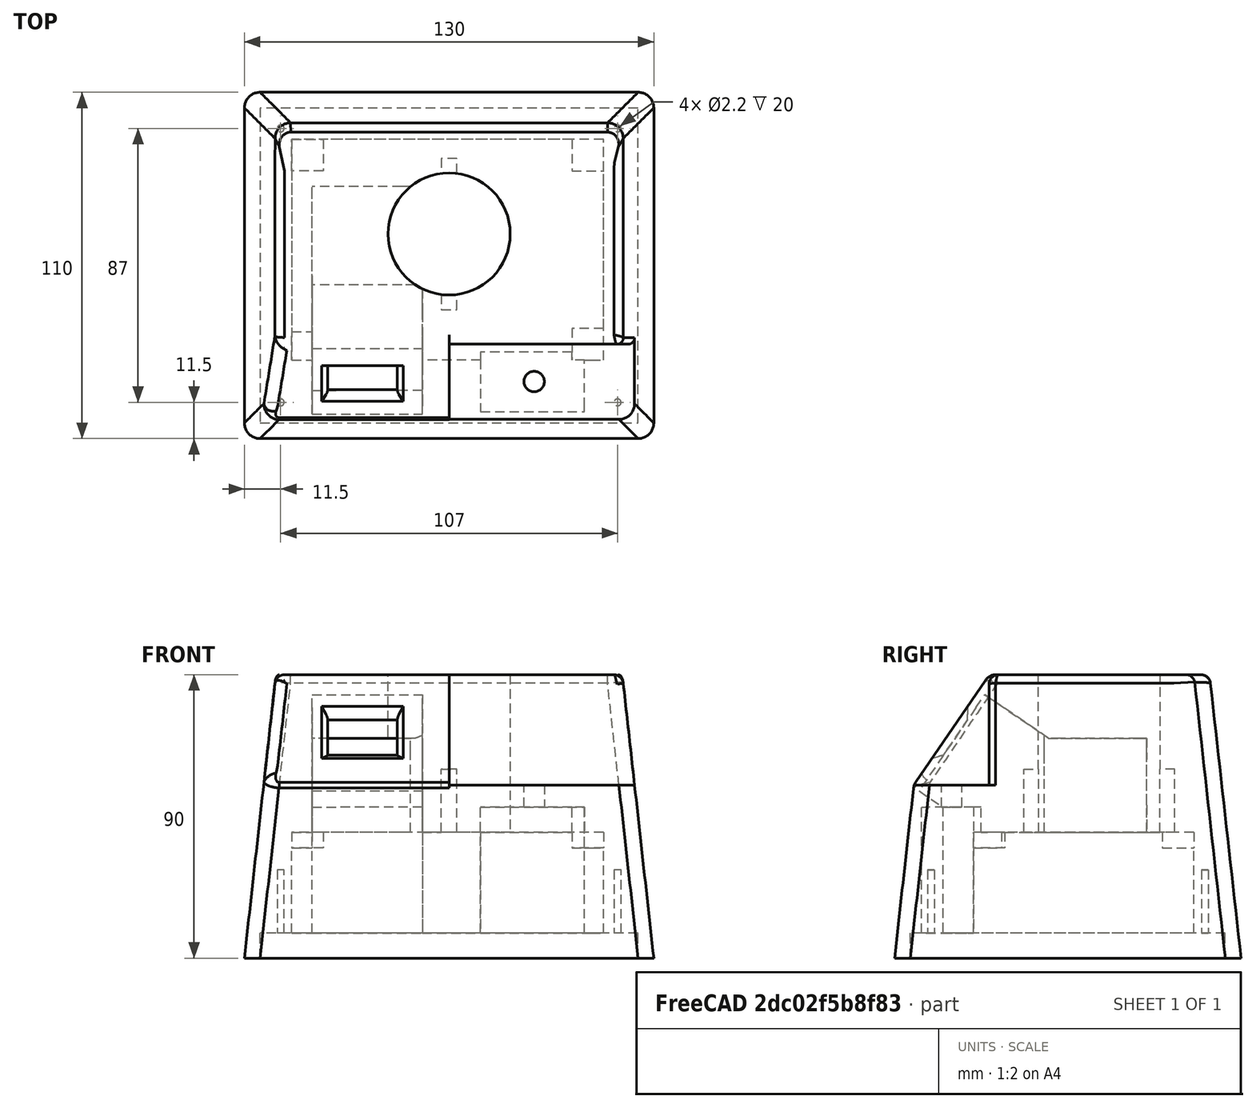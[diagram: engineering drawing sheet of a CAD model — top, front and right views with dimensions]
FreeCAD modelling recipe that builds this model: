
FCSTD DOCUMENT  (FreeCAD 0.17R13541 (Git))
Label: newDesign
License: All rights reserved
LicenseURL: http://en.wikipedia.org/wiki/All_rights_reserved
objects: PartDesign::Pocket×33, Sketcher::SketchObject×31, PartDesign::Plane×17, PartDesign::Pad×11, PartDesign::Fillet×9, PartDesign::Chamfer×2, PartDesign::AdditiveLoft×1, PartDesign::Body×1, Mesh::Feature×1
note: 150 computed .brp shape members not serialized (recipe doc carries the construction recipe); baked Part::Feature solids carry a one-line shape summary decoded from their .brp

FEATURE [Sketcher::SketchObject] Sketch
  MapMode = 5
  Support = -> [XY_Plane]
  sketch-geometry (4):
    g0: LineSegment StartX=0 StartY=110 StartZ=0 EndX=130 EndY=110 EndZ=0
    g1: LineSegment StartX=130 StartY=110 StartZ=0 EndX=130 EndY=0 EndZ=0
    g2: LineSegment StartX=130 StartY=0 StartZ=0 EndX=0 EndY=0 EndZ=0
    g3: LineSegment StartX=0 StartY=0 StartZ=0 EndX=0 EndY=110 EndZ=0
  constraints (11):
    c: Coincident(g0,g1)
    c: Coincident(g1,g2)
    c: Coincident(g2,g3)
    c: Coincident(g3,g0)
    c: Horizontal(g0)
    c: Horizontal(g2)
    c: Vertical(g1)
    c: Vertical(g3)
    c: Distance(g0) = 130
    c: Distance(g1) = 110
    c: Coincident(g-1,g2)
FEATURE [PartDesign::Plane] DatumPlane
  AttachmentOffset = pos=(0,90,0) rot=(1,0,0;1.5708rad)
  MapMode = 7
  Placement = pos=(0,110,90) rot=(0.707107,-0.707107,0;3.14159rad)
  Support = -> [Sketch]
FEATURE [Sketcher::SketchObject] Sketch001
  MapMode = 5
  Placement = pos=(0,110,90) rot=(-0.707107,0.707107,0;3.14159rad)
  Support = -> [DatumPlane]
  sketch-geometry (4):
    g0: LineSegment StartX=10 StartY=-10 StartZ=0 EndX=100 EndY=-10 EndZ=0
    g1: LineSegment StartX=100 StartY=-10 StartZ=0 EndX=100 EndY=-120 EndZ=0
    g2: LineSegment StartX=100 StartY=-120 StartZ=0 EndX=10 EndY=-120 EndZ=0
    g3: LineSegment StartX=10 StartY=-120 StartZ=0 EndX=10 EndY=-10 EndZ=0
  constraints (12):
    c: Coincident(g0,g1)
    c: Coincident(g1,g2)
    c: Coincident(g2,g3)
    c: Coincident(g3,g0)
    c: Horizontal(g0)
    c: Horizontal(g2)
    c: Vertical(g1)
    c: Vertical(g3)
    c: DistanceX(g0,g0) = 90
    c: DistanceY(g1,g1) = 110
    c: DistanceY(g0,g-1) = 10
    c: DistanceX(g-1,g0) = 10
FEATURE [PartDesign::AdditiveLoft] AdditiveLoft
  Closed = false
  Profile = -> Sketch
  Ruled = false
  Sections = -> [Sketch001]
FEATURE [PartDesign::Plane] DatumPlane001
  MapMode = 5
  Placement = pos=(0,0,90) rot=(0,0,1;0rad)
  Support = -> [AdditiveLoft]
FEATURE [Sketcher::SketchObject] Sketch002
  MapMode = 5
  Placement = pos=(0,0,90) rot=(0,0,1;0rad)
  Support = -> [DatumPlane001]
  sketch-geometry (4):
    g0: LineSegment StartX=65 StartY=30 StartZ=0 EndX=130 EndY=30 EndZ=0
    g1: LineSegment StartX=130 StartY=30 StartZ=0 EndX=130 EndY=0 EndZ=0
    g2: LineSegment StartX=130 StartY=0 StartZ=0 EndX=65 EndY=0 EndZ=0
    g3: LineSegment StartX=65 StartY=0 StartZ=0 EndX=65 EndY=30 EndZ=0
  constraints (12):
    c: Coincident(g0,g1)
    c: Coincident(g1,g2)
    c: Coincident(g2,g3)
    c: Coincident(g3,g0)
    c: Horizontal(g0)
    c: Horizontal(g2)
    c: Vertical(g1)
    c: Vertical(g3)
    c: DistanceX(g-1,g2) = 65
    c: DistanceY(g1,g1) = 30
    c: DistanceY(g-1,g2) = 0
    c: DistanceX(g0,g0) = 65
FEATURE [PartDesign::Pocket] Pocket
  BaseFeature = -> AdditiveLoft
  Length = 35
  Length2 = 100
  Profile = -> Sketch002
  Type = 0
FEATURE [PartDesign::Plane] DatumPlane002
  MapMode = 5
  Placement = pos=(65,0,0) rot=(0.57735,0.57735,0.57735;2.0944rad)
  Support = -> [Pocket]
FEATURE [Sketcher::SketchObject] Sketch003
  ExternalGeometry = -> [Pocket]
  MapMode = 5
  Placement = pos=(65,0,0) rot=(0.57735,0.57735,0.57735;2.0944rad)
  Support = -> [DatumPlane002]
  sketch-geometry (3):
    g0: LineSegment StartX=6.11111 StartY=55 StartZ=0 EndX=30 EndY=90 EndZ=0
    g1: LineSegment StartX=30 StartY=90 StartZ=0 EndX=10 EndY=90 EndZ=0
    g2: LineSegment StartX=10 StartY=90 StartZ=0 EndX=6.11111 EndY=55 EndZ=0
  constraints (7):
    c: Coincident(g0,g1)
    c: Horizontal(g1)
    c: Coincident(g1,g2)
    c: Coincident(g2,g0)
    c: Coincident(g0,g-3)
    c: Coincident(g1,g-5)
    c: Coincident(g0,g-4)
FEATURE [PartDesign::Pocket] Pocket001
  BaseFeature = -> Pocket
  Length = 60
  Length2 = 100
  Profile = -> Sketch003
  Type = 0
FEATURE [Sketcher::SketchObject] Sketch004
  MapMode = 5
  Placement = pos=(0,0,55) rot=(0,0,1;0rad)
  Support = -> [Pocket001]
FEATURE [PartDesign::Plane] DatumPlane003
  MapMode = 5
  Placement = pos=(0,0,55) rot=(0,0,1;0rad)
  Support = -> [Pocket001]
FEATURE [Sketcher::SketchObject] Sketch005
  ExternalGeometry = -> [Pocket001]
  MapMode = 5
  Placement = pos=(0,0,55) rot=(0,0,1;0rad)
  Support = -> [DatumPlane003]
  sketch-geometry (1):
    g0: Circle CenterX=92 CenterY=18.1111 CenterZ=0 NormalX=0 NormalY=0 NormalZ=1 AngleXU=0 Radius=3.25
  constraints (3):
    c: Radius(g0) = 3.25
    c: DistanceX(g-3,g0) = 27
    c: DistanceY(g-3,g0) = 12
FEATURE [PartDesign::Pad] Pad
  BaseFeature = -> Pocket001
  Length = 10
  Length2 = 100
  Profile = -> Sketch005
  Type = 0
FEATURE [PartDesign::Plane] DatumPlane004
  MapMode = 5
  Placement = pos=(0,-21.4404,14.6339) rot=(1,0,0;0.971885rad)
  Support = -> [Pad]
FEATURE [Sketcher::SketchObject] Sketch006
  ExternalGeometry = -> [Pad]
  MapMode = 5
  Placement = pos=(0,-21.4404,14.6339) rot=(1,0,0;0.971885rad)
  Support = -> [DatumPlane004]
  sketch-geometry (4):
    g0: LineSegment StartX=26.5 StartY=74.6655 StartZ=0 EndX=48.5 EndY=74.6655 EndZ=0
    g1: LineSegment StartX=48.5 StartY=74.6655 StartZ=0 EndX=48.5 EndY=62.6655 EndZ=0
    g2: LineSegment StartX=48.5 StartY=62.6655 StartZ=0 EndX=26.5 EndY=62.6655 EndZ=0
    g3: LineSegment StartX=26.5 StartY=62.6655 StartZ=0 EndX=26.5 EndY=74.6655 EndZ=0
  constraints (11):
    c: Coincident(g0,g1)
    c: Coincident(g1,g2)
    c: Coincident(g2,g3)
    c: Coincident(g3,g0)
    c: Horizontal(g0)
    c: Horizontal(g2)
    c: Vertical(g1)
    c: Vertical(g3)
    c: DistanceX(g0,g0) = 22
    c: DistanceY(g3,g3) = 12
    c: DistanceX(g-4,g0) = 16.5
FEATURE [PartDesign::Pocket] Pocket002
  BaseFeature = -> Pad
  Length = 3
  Length2 = 100
  Profile = -> Sketch006
  Type = 0
FEATURE [PartDesign::Plane] DatumPlane005
  MapMode = 5
  Placement = pos=(48.5,0,0) rot=(0.57735,-0.57735,-0.57735;2.0944rad)
  Support = -> [Pocket002]
FEATURE [Sketcher::SketchObject] Sketch007
  ExternalGeometry = -> [Pocket002]
  MapMode = 5
  Placement = pos=(48.5,0,0) rot=(0.57735,-0.57735,-0.57735;2.0944rad)
  Support = -> [DatumPlane005]
  sketch-geometry (4):
    g0: LineSegment StartX=-23.1297 StartY=74.6127 StartZ=0 EndX=-20.6519 EndY=76.3039 EndZ=0
    g1: LineSegment StartX=-20.6519 StartY=76.3039 StartZ=0 EndX=-20.6519 EndY=81.3039 EndZ=0
    g2: LineSegment StartX=-20.6519 StartY=81.3039 StartZ=0 EndX=-23.1297 EndY=81.3039 EndZ=0
    g3: LineSegment StartX=-23.1297 StartY=81.3039 StartZ=0 EndX=-23.1297 EndY=74.6127 EndZ=0
  constraints (10):
    c: Coincident(g0,g1)
    c: Vertical(g1)
    c: Coincident(g1,g2)
    c: Horizontal(g2)
    c: Coincident(g2,g3)
    c: Vertical(g3)
    c: Coincident(g3,g0)
    c: Coincident(g0,g-4)
    c: Coincident(g-3,g0)
    c: DistanceY(g1,g1) = 5
FEATURE [PartDesign::Pocket] Pocket003
  BaseFeature = -> Pocket002
  Length = 22
  Length2 = 100
  Profile = -> Sketch007
  Reversed = true
  Type = 0
FEATURE [PartDesign::Plane] DatumPlane006
  MapMode = 5
  Placement = pos=(48.5,0,0) rot=(0.57735,-0.57735,-0.57735;2.0944rad)
  Support = -> [Pocket003]
FEATURE [Sketcher::SketchObject] Sketch008
  MapMode = 5
  Placement = pos=(48.5,0,0) rot=(0.57735,-0.57735,-0.57735;2.0944rad)
  Support = -> [DatumPlane006]
FEATURE [Sketcher::SketchObject] Sketch009
  ExternalGeometry = -> [Pocket003]
  MapMode = 5
  Placement = pos=(48.5,0,0) rot=(0.57735,-0.57735,-0.57735;2.0944rad)
  Support = -> [DatumPlane006]
  sketch-geometry (3):
    g0: LineSegment StartX=-16.3648 StartY=64.7013 StartZ=0 EndX=-16.3648 EndY=74.7013 EndZ=0
    g1: LineSegment StartX=-16.3648 StartY=74.7013 StartZ=0 EndX=-7.90863 EndY=62.312 EndZ=0
    g2: LineSegment StartX=-7.90863 StartY=62.312 StartZ=0 EndX=-16.3648 EndY=64.7013 EndZ=0
  constraints (8):
    c: Vertical(g0)
    c: Coincident(g0,g1)
    c: Coincident(g2,g0)
    c: Parallel(g1,g-4)
    c: Distance(g0) = 10
    c: Coincident(g0,g-3)
    c: Coincident(g2,g1)
    c: Distance(g1) = 15
FEATURE [PartDesign::Pocket] Pocket004
  BaseFeature = -> Pocket003
  Length = 22
  Length2 = 100
  Profile = -> Sketch009
  Reversed = true
  Type = 0
FEATURE [PartDesign::Chamfer] Chamfer
  Base = -> Pocket004 [Edge26,Edge27,Edge28,Edge29]
  BaseFeature = -> Pocket004
  Size = 2
FEATURE [PartDesign::Fillet] Fillet
  Base = -> Chamfer [Edge31,Edge27,Edge24,Edge21]
  BaseFeature = -> Chamfer
  Radius = 2
FEATURE [PartDesign::Chamfer] Chamfer001
  Base = -> Fillet [Edge22,Edge20,Edge17,Edge24]
  BaseFeature = -> Fillet
  Size = 2
FEATURE [PartDesign::Fillet] Fillet001
  Base = -> Chamfer001 [Edge10,Edge36,Edge44,Edge54]
  BaseFeature = -> Chamfer001
  Radius = 2
FEATURE [PartDesign::Fillet] Fillet002
  Base = -> Fillet001 [Edge91]
  BaseFeature = -> Fillet001
  Radius = 5
FEATURE [PartDesign::Fillet] Fillet003
  Base = -> Fillet002 [Edge17]
  BaseFeature = -> Fillet002
  Radius = 5
FEATURE [PartDesign::Fillet] Fillet004
  Base = -> Fillet003 [Edge18]
  BaseFeature = -> Fillet003
  Radius = 2
FEATURE [PartDesign::Fillet] Fillet005
  Base = -> Fillet004 [Edge43]
  BaseFeature = -> Fillet004
  Radius = 5
FEATURE [PartDesign::Fillet] Fillet006
  Base = -> Fillet005 [Edge23]
  BaseFeature = -> Fillet005
  Radius = 5
FEATURE [PartDesign::Plane] DatumPlane007
  MapMode = 5
  Placement = pos=(0,0,90) rot=(0,0,1;0rad)
  Support = -> [Fillet006]
FEATURE [Sketcher::SketchObject] Sketch010
  ExternalGeometry = -> [Sketch001,Fillet006]
  MapMode = 5
  Placement = pos=(0,0,90) rot=(0,0,1;0rad)
  Support = -> [DatumPlane007]
  sketch-geometry (1):
    g0: Circle CenterX=65 CenterY=65 CenterZ=0 NormalX=0 NormalY=0 NormalZ=1 AngleXU=0 Radius=2
  constraints (3):
    c: Radius(g0) = 2
    c: DistanceX(g-3,g0) = 55
    c: DistanceY(g-6,g0) = 35
FEATURE [PartDesign::Pad] Pad001
  BaseFeature = -> Fillet006
  Length = 10
  Length2 = 100
  Profile = -> Sketch010
  Type = 0
FEATURE [PartDesign::Plane] DatumPlane008
  MapMode = 5
  Placement = pos=(0,0,100) rot=(0,0,1;0rad)
  Support = -> [Pad001]
FEATURE [Sketcher::SketchObject] Sketch011
  ExternalGeometry = -> [Pad001]
  MapMode = 5
  Placement = pos=(0,0,100) rot=(0,0,1;0rad)
  Support = -> [DatumPlane008]
  sketch-geometry (1):
    g0: Circle CenterX=65 CenterY=65 CenterZ=0 NormalX=0 NormalY=0 NormalZ=1 AngleXU=0 Radius=19.4
  constraints (2):
    c: Coincident(g0,g-3)
    c: Radius(g0) = 19.4
FEATURE [PartDesign::Pocket] Pocket005
  BaseFeature = -> Pad001
  Length = 100
  Length2 = 100
  Profile = -> Sketch011
  Type = 0
FEATURE [Sketcher::SketchObject] Sketch012
  MapMode = 5
  Placement = pos=(0,0,65) rot=(0,0,1;0rad)
  Support = -> [Pocket005]
FEATURE [PartDesign::Pocket] Pocket006
  BaseFeature = -> Pocket005
  Length = 68
  Length2 = 100
  Profile = -> Pocket005 [Face28]
  Type = 0
FEATURE [PartDesign::Plane] DatumPlane009
  MapMode = 5
  Placement = pos=(0,0,0) rot=(1,0,0;3.14159rad)
  Support = -> [Pocket006]
FEATURE [Sketcher::SketchObject] Sketch013
  MapMode = 5
  Placement = pos=(0,0,0) rot=(1,0,0;3.14159rad)
  Support = -> [DatumPlane009]
  sketch-geometry (4):
    g0: LineSegment StartX=15 StartY=-25 StartZ=0 EndX=114 EndY=-25 EndZ=0
    g1: LineSegment StartX=114 StartY=-25 StartZ=0 EndX=114 EndY=-95 EndZ=0
    g2: LineSegment StartX=114 StartY=-95 StartZ=0 EndX=15 EndY=-95 EndZ=0
    g3: LineSegment StartX=15 StartY=-95 StartZ=0 EndX=15 EndY=-25 EndZ=0
  constraints (12):
    c: Coincident(g0,g1)
    c: Coincident(g1,g2)
    c: Coincident(g2,g3)
    c: Coincident(g3,g0)
    c: Horizontal(g0)
    c: Horizontal(g2)
    c: Vertical(g1)
    c: Vertical(g3)
    c: DistanceX(g0,g0) = 99
    c: DistanceY(g1,g1) = 70
    c: DistanceY(g0,g-1) = 25
    c: DistanceX(g-1,g0) = 15
FEATURE [PartDesign::Pocket] Pocket007
  BaseFeature = -> Pocket006
  Length = 40
  Length2 = 100
  Profile = -> Sketch013
  Type = 0
FEATURE [PartDesign::Pocket] Pocket008
  BaseFeature = -> Pocket007
  Length = 64
  Length2 = 100
  Profile = -> Pocket007 [Face34]
  Type = 0
FEATURE [PartDesign::Plane] DatumPlane010
  MapMode = 5
  Placement = pos=(0,0,0) rot=(1,0,0;3.14159rad)
  Support = -> [Pocket008]
FEATURE [Sketcher::SketchObject] Sketch014
  MapMode = 5
  Placement = pos=(0,0,0) rot=(1,0,0;3.14159rad)
  Support = -> [DatumPlane010]
  sketch-geometry (4):
    g0: LineSegment StartX=75 StartY=-10 StartZ=0 EndX=110 EndY=-10 EndZ=0
    g1: LineSegment StartX=110 StartY=-10 StartZ=0 EndX=110 EndY=-27.5 EndZ=0
    g2: LineSegment StartX=110 StartY=-27.5 StartZ=0 EndX=75 EndY=-27.5 EndZ=0
    g3: LineSegment StartX=75 StartY=-27.5 StartZ=0 EndX=75 EndY=-10 EndZ=0
  constraints (12):
    c: Coincident(g0,g1)
    c: Coincident(g1,g2)
    c: Coincident(g2,g3)
    c: Coincident(g3,g0)
    c: Horizontal(g0)
    c: Horizontal(g2)
    c: Vertical(g1)
    c: Vertical(g3)
    c: DistanceX(g0,g0) = 35
    c: DistanceX(g-1,g0) = 75
    c: DistanceY(g1,g1) = 17.5
    c: DistanceY(g0,g-1) = 10
FEATURE [PartDesign::Pocket] Pocket009
  BaseFeature = -> Pocket008
  Length = 48
  Length2 = 100
  Profile = -> Sketch014
  Type = 0
FEATURE [PartDesign::Plane] DatumPlane011
  MapMode = 5
  Placement = pos=(0,0,40) rot=(1,0,0;3.14159rad)
  Support = -> [Pocket009]
FEATURE [Sketcher::SketchObject] Sketch015
  ExternalGeometry = -> [Pocket009]
  MapMode = 5
  Placement = pos=(0,0,40) rot=(1,0,0;3.14159rad)
  Support = -> [DatumPlane011]
  sketch-geometry (4):
    g0: LineSegment StartX=20 StartY=-40 StartZ=0 EndX=50 EndY=-40 EndZ=0
    g1: LineSegment StartX=50 StartY=-40 StartZ=0 EndX=50 EndY=-80 EndZ=0
    g2: LineSegment StartX=50 StartY=-80 StartZ=0 EndX=20 EndY=-80 EndZ=0
    g3: LineSegment StartX=20 StartY=-80 StartZ=0 EndX=20 EndY=-40 EndZ=0
  constraints (12):
    c: Coincident(g0,g1)
    c: Coincident(g1,g2)
    c: Coincident(g2,g3)
    c: Coincident(g3,g0)
    c: Horizontal(g0)
    c: Horizontal(g2)
    c: Vertical(g1)
    c: Vertical(g3)
    c: DistanceX(g0,g0) = 30
    c: DistanceX(g-3,g0) = 5
    c: DistanceY(g1,g1) = 40
    c: DistanceY(g0,g-3) = 15
FEATURE [PartDesign::Pocket] Pocket010
  BaseFeature = -> Pocket009
  Length = 31
  Length2 = 100
  Profile = -> Sketch015
  Type = 0
FEATURE [Sketcher::SketchObject] Sketch016
  ExternalGeometry = -> [Pocket010]
  MapMode = 5
  Placement = pos=(26.5,0,0) rot=(0.57735,0.57735,0.57735;2.0944rad)
  Support = -> [Pocket010]
  sketch-geometry (3):
    g0: LineSegment StartX=40 StartY=63.098 StartZ=0 EndX=33.2351 EndY=53.1866 EndZ=0
    g1: LineSegment StartX=33.2351 StartY=53.1866 StartZ=0 EndX=40 EndY=48.5693 EndZ=0
    g2: LineSegment StartX=40 StartY=48.5693 StartZ=0 EndX=40 EndY=63.098 EndZ=0
  constraints (7):
    c: Coincident(g0,g1)
    c: Coincident(g1,g2)
    c: Coincident(g2,g0)
    c: Coincident(g0,g-5)
    c: Coincident(g-4,g1)
    c: Parallel(g0,g-3)
    c: Parallel(g1,g-6)
FEATURE [PartDesign::Pocket] Pocket011
  BaseFeature = -> Pocket010
  Length = 5
  Length2 = 100
  Profile = -> Sketch016
  Type = 0
FEATURE [PartDesign::Plane] DatumPlane012
  MapMode = 5
  Placement = pos=(0,-2.09222,1.42802) rot=(0,0.884235,0.467042;3.14159rad)
  Support = -> [Pocket011]
FEATURE [Sketcher::SketchObject] Sketch017
  ExternalGeometry = -> [Pocket011]
  MapMode = 5
  Placement = pos=(0,-2.09222,1.42802) rot=(0,0.884235,0.467042;3.14159rad)
  Support = -> [DatumPlane012]
  sketch-geometry (4):
    g0: LineSegment StartX=-21.5 StartY=74.6655 StartZ=0 EndX=-56.5 EndY=74.6655 EndZ=0
    g1: LineSegment StartX=-56.5 StartY=74.6655 StartZ=0 EndX=-56.5 EndY=49.6655 EndZ=0
    g2: LineSegment StartX=-56.5 StartY=49.6655 StartZ=0 EndX=-21.5 EndY=49.6655 EndZ=0
    g3: LineSegment StartX=-21.5 StartY=49.6655 StartZ=0 EndX=-21.5 EndY=74.6655 EndZ=0
  constraints (11):
    c: Coincident(g0,g1)
    c: Coincident(g1,g2)
    c: Coincident(g2,g3)
    c: Coincident(g3,g0)
    c: Horizontal(g0)
    c: Horizontal(g2)
    c: Vertical(g1)
    c: Vertical(g3)
    c: Coincident(g0,g-3)
    c: DistanceX(g0,g0) = 35
    c: DistanceY(g3,g3) = 25
FEATURE [PartDesign::Pocket] Pocket012
  BaseFeature = -> Pocket011
  Length = 25
  Length2 = 100
  Profile = -> Sketch017
  Reversed = true
  Type = 0
FEATURE [Sketcher::SketchObject] Sketch018
  ExternalGeometry = -> [Pocket012]
  MapMode = 5
  Placement = pos=(0,0,40) rot=(1,0,0;3.14159rad)
  Support = -> [Pocket012]
  sketch-geometry (4):
    g0: LineSegment StartX=56.5 StartY=-29.4949 StartZ=0 EndX=21.5 EndY=-29.4949 EndZ=0
    g1: LineSegment StartX=21.5 StartY=-29.4949 StartZ=0 EndX=21.5 EndY=-25 EndZ=0
    g2: LineSegment StartX=21.5 StartY=-25 StartZ=0 EndX=56.5 EndY=-25 EndZ=0
    g3: LineSegment StartX=56.5 StartY=-25 StartZ=0 EndX=56.5 EndY=-29.4949 EndZ=0
  constraints (11):
    c: Coincident(g0,g1)
    c: Coincident(g1,g2)
    c: Coincident(g2,g3)
    c: Coincident(g3,g0)
    c: Horizontal(g0)
    c: Horizontal(g2)
    c: Vertical(g1)
    c: Vertical(g3)
    c: Coincident(g0,g-3)
    c: Coincident(g0,g-4)
    c: DistanceY(g1,g-5) = 0
FEATURE [PartDesign::Pocket] Pocket013
  BaseFeature = -> Pocket012
  Length = 5
  Length2 = 100
  Profile = -> Sketch018
  Type = 0
FEATURE [Sketcher::SketchObject] Sketch019
  ExternalGeometry = -> [Pocket013]
  MapMode = 5
  Placement = pos=(0,-2.09222,1.42802) rot=(0,0.884235,0.467042;3.14159rad)
  Support = -> [Pocket013]
  sketch-geometry (4):
    g0: LineSegment StartX=-56.5 StartY=80.2538 StartZ=0 EndX=-21.5 EndY=80.2538 EndZ=0
    g1: LineSegment StartX=-21.5 StartY=80.2538 StartZ=0 EndX=-21.5 EndY=52.7538 EndZ=0
    g2: LineSegment StartX=-21.5 StartY=52.7538 StartZ=0 EndX=-56.5 EndY=52.7538 EndZ=0
    g3: LineSegment StartX=-56.5 StartY=52.7538 StartZ=0 EndX=-56.5 EndY=80.2538 EndZ=0
  constraints (11):
    c: Coincident(g0,g1)
    c: Coincident(g1,g2)
    c: Coincident(g2,g3)
    c: Coincident(g3,g0)
    c: Horizontal(g0)
    c: Horizontal(g2)
    c: Vertical(g1)
    c: Vertical(g3)
    c: Coincident(g-3,g2)
    c: DistanceX(g2,g2) = 35
    c: DistanceY(g1,g1) = 27.5
FEATURE [PartDesign::Pocket] Pocket014
  BaseFeature = -> Pocket013
  Length = 19
  Length2 = 100
  Profile = -> Sketch019
  Type = 0
FEATURE [PartDesign::Pocket] Pocket015
  BaseFeature = -> Pocket014
  Length = 20
  Length2 = 100
  Profile = -> Sketch019
  Reversed = true
  Type = 0
FEATURE [Sketcher::SketchObject] Sketch020
  ExternalGeometry = -> [Pocket015]
  MapMode = 5
  Placement = pos=(0,0,71) rot=(1,0,0;3.14159rad)
  Support = -> [Pocket015]
  sketch-geometry (4):
    g0: LineSegment StartX=20 StartY=-40 StartZ=0 EndX=56.5 EndY=-40 EndZ=0
    g1: LineSegment StartX=56.5 StartY=-40 StartZ=0 EndX=56.5 EndY=-80 EndZ=0
    g2: LineSegment StartX=56.5 StartY=-80 StartZ=0 EndX=20 EndY=-80 EndZ=0
    g3: LineSegment StartX=20 StartY=-80 StartZ=0 EndX=20 EndY=-40 EndZ=0
  constraints (11):
    c: Coincident(g0,g1)
    c: Coincident(g1,g2)
    c: Coincident(g2,g3)
    c: Coincident(g3,g0)
    c: Horizontal(g0)
    c: Horizontal(g2)
    c: Vertical(g1)
    c: Vertical(g3)
    c: Coincident(g2,g-4)
    c: Coincident(g-3,g0)
    c: DistanceX(g0,g-5) = 0
FEATURE [PartDesign::Pocket] Pocket016
  BaseFeature = -> Pocket015
  Length = 39
  Length2 = 100
  Profile = -> Sketch020
  Reversed = true
  Type = 0
FEATURE [PartDesign::Pad] Pad002
  BaseFeature = -> Pocket016
  Length = 40
  Length2 = 100
  Profile = -> Pocket016 [Face75]
  Type = 0
FEATURE [PartDesign::Pad] Pad003
  BaseFeature = -> Pad002
  Length = 40
  Length2 = 100
  Profile = -> Pad002 [Face80]
  Type = 0
FEATURE [PartDesign::Pocket] Pocket017
  BaseFeature = -> Pad003
  Length = 5
  Length2 = 100
  Profile = -> Pad003 [Face79]
  Type = 0
FEATURE [PartDesign::Pocket] Pocket018
  BaseFeature = -> Pocket017
  Length = 5
  Length2 = 100
  Profile = -> Pocket017 [Face60]
  Type = 0
FEATURE [PartDesign::Pocket] Pocket019
  BaseFeature = -> Pocket018
  Length = 5
  Length2 = 100
  Profile = -> Pocket018 [Face81]
  Type = 0
FEATURE [PartDesign::Pad] Pad004
  BaseFeature = -> Pocket019
  Length = 10
  Length2 = 100
  Profile = -> Pocket019 [Face83]
  Type = 0
FEATURE [PartDesign::Pocket] Pocket020
  BaseFeature = -> Pad004
  Length = 5
  Length2 = 100
  Profile = -> Pad004 [Face60]
  Type = 0
FEATURE [PartDesign::Pocket] Pocket021
  BaseFeature = -> Pocket020
  Length = 1
  Length2 = 100
  Profile = -> Pocket020 [Face65]
  Type = 0
FEATURE [PartDesign::Pocket] Pocket022
  BaseFeature = -> Pocket021
  Length = 1
  Length2 = 100
  Profile = -> Pocket021 [Face65]
  Type = 0
FEATURE [Sketcher::SketchObject] Sketch021
  ExternalGeometry = -> [Pocket022]
  MapMode = 5
  Placement = pos=(0,45.2426,66.2856) rot=(1,0,0;2.54268rad)
  Support = -> [Pocket022]
  sketch-geometry (4):
    g0: LineSegment StartX=21.5 StartY=23.5331 StartZ=0 EndX=56.5 EndY=23.5331 EndZ=0
    g1: LineSegment StartX=56.5 StartY=23.5331 StartZ=0 EndX=56.5 EndY=-1.46689 EndZ=0
    g2: LineSegment StartX=56.5 StartY=-1.46689 StartZ=0 EndX=21.5 EndY=-1.46689 EndZ=0
    g3: LineSegment StartX=21.5 StartY=-1.46689 StartZ=0 EndX=21.5 EndY=23.5331 EndZ=0
  constraints (11):
    c: Coincident(g0,g1)
    c: Coincident(g1,g2)
    c: Coincident(g2,g3)
    c: Coincident(g3,g0)
    c: Horizontal(g0)
    c: Horizontal(g2)
    c: Vertical(g1)
    c: Vertical(g3)
    c: Coincident(g0,g-3)
    c: Coincident(g0,g-4)
    c: DistanceY(g1,g1) = 25
FEATURE [PartDesign::Pocket] Pocket023
  BaseFeature = -> Pocket022
  Length = 5
  Length2 = 100
  Profile = -> Sketch021
  Type = 0
FEATURE [PartDesign::Plane] DatumPlane013
  MapMode = 5
  Placement = pos=(0,-19.4372,13.2666) rot=(0,0.884235,0.467042;3.14159rad)
  Support = -> [Pocket023]
FEATURE [Sketcher::SketchObject] Sketch022
  ExternalGeometry = -> [Pocket023]
  MapMode = 5
  Placement = pos=(0,-19.4372,13.2666) rot=(0,0.884235,0.467042;3.14159rad)
  Support = -> [DatumPlane013]
  sketch-geometry (4):
    g0: LineSegment StartX=-56.5 StartY=85.2538 StartZ=0 EndX=-21.5 EndY=85.2538 EndZ=0
    g1: LineSegment StartX=-21.5 StartY=85.2538 StartZ=0 EndX=-21.5 EndY=48.2538 EndZ=0
    g2: LineSegment StartX=-21.5 StartY=48.2538 StartZ=0 EndX=-56.5 EndY=48.2538 EndZ=0
    g3: LineSegment StartX=-56.5 StartY=48.2538 StartZ=0 EndX=-56.5 EndY=85.2538 EndZ=0
  constraints (11):
    c: Coincident(g0,g1)
    c: Coincident(g1,g2)
    c: Coincident(g2,g3)
    c: Coincident(g3,g0)
    c: Horizontal(g0)
    c: Horizontal(g2)
    c: Vertical(g1)
    c: Vertical(g3)
    c: Coincident(g0,g-3)
    c: Coincident(g0,g-4)
    c: DistanceY(g1,g1) = 37
FEATURE [PartDesign::Pocket] Pocket024
  BaseFeature = -> Pocket023
  Length = 28
  Length2 = 100
  Profile = -> Sketch022
  Reversed = true
  Type = 0
FEATURE [PartDesign::Plane] DatumPlane014
  MapMode = 5
  Placement = pos=(0,0,0) rot=(1,0,0;3.14159rad)
  Support = -> [Pocket024]
FEATURE [Sketcher::SketchObject] Sketch023
  ExternalGeometry = -> [Pocket024]
  MapMode = 5
  Placement = pos=(0,0,0) rot=(1,0,0;3.14159rad)
  Support = -> [DatumPlane014]
  sketch-geometry (4):
    g0: LineSegment StartX=75 StartY=-25 StartZ=0 EndX=30 EndY=-25 EndZ=0
    g1: LineSegment StartX=30 StartY=-25 StartZ=0 EndX=30 EndY=-10 EndZ=0
    g2: LineSegment StartX=30 StartY=-10 StartZ=0 EndX=75 EndY=-10 EndZ=0
    g3: LineSegment StartX=75 StartY=-10 StartZ=0 EndX=75 EndY=-25 EndZ=0
  constraints (11):
    c: Coincident(g0,g1)
    c: Coincident(g1,g2)
    c: Coincident(g2,g3)
    c: Coincident(g3,g0)
    c: Horizontal(g0)
    c: Horizontal(g2)
    c: Vertical(g1)
    c: Vertical(g3)
    c: Coincident(g0,g-3)
    c: Coincident(g2,g-4)
    c: DistanceX(g0,g0) = 45
FEATURE [PartDesign::Pocket] Pocket025
  BaseFeature = -> Pocket024
  Length = 48
  Length2 = 100
  Profile = -> Sketch023
  Type = 0
FEATURE [PartDesign::Pocket] Pocket026
  BaseFeature = -> Pocket025
  Length = 34
  Length2 = 100
  Profile = -> Pocket025 [Face54]
  Type = 0
FEATURE [PartDesign::Pad] Pad005
  BaseFeature = -> Pocket026
  Length = 2
  Length2 = 100
  Profile = -> Pocket026 [Face29]
  Type = 0
FEATURE [PartDesign::Pad] Pad006
  BaseFeature = -> Pad005
  Length = 8
  Length2 = 100
  Profile = -> Pad005 [Face55]
  Type = 0
FEATURE [PartDesign::Pad] Pad007
  BaseFeature = -> Pad006
  Length = 48
  Length2 = 100
  Profile = -> Pad006 [Face53]
  Type = 0
FEATURE [PartDesign::Plane] DatumPlane015
  MapMode = 5
  Placement = pos=(0,0,40) rot=(1,0,0;3.14159rad)
  Support = -> [Pad007]
FEATURE [Sketcher::SketchObject] Sketch024
  ExternalGeometry = -> [Pad007]
  MapMode = 5
  Placement = pos=(0,0,40) rot=(1,0,0;3.14159rad)
  Support = -> [DatumPlane015]
  sketch-geometry (4):
    g0: LineSegment StartX=104 StartY=-25 StartZ=0 EndX=114 EndY=-25 EndZ=0
    g1: LineSegment StartX=114 StartY=-25 StartZ=0 EndX=114 EndY=-35 EndZ=0
    g2: LineSegment StartX=114 StartY=-35 StartZ=0 EndX=104 EndY=-35 EndZ=0
    g3: LineSegment StartX=104 StartY=-35 StartZ=0 EndX=104 EndY=-25 EndZ=0
  constraints (11):
    c: Coincident(g0,g1)
    c: Coincident(g1,g2)
    c: Coincident(g2,g3)
    c: Coincident(g3,g0)
    c: Horizontal(g0)
    c: Horizontal(g2)
    c: Vertical(g1)
    c: Vertical(g3)
    c: Coincident(g0,g-3)
    c: DistanceX(g0,g0) = 10
    c: DistanceY(g3,g3) = 10
FEATURE [PartDesign::Pad] Pad008
  BaseFeature = -> Pad007
  Length = 10
  Length2 = 100
  Profile = -> Sketch024
  Reversed = true
  Type = 0
FEATURE [PartDesign::Pad] Pad009
  BaseFeature = -> Pad008
  Length = 5
  Length2 = 100
  Profile = -> Sketch024
  Type = 0
FEATURE [Sketcher::SketchObject] Sketch025
  ExternalGeometry = -> [Pad009]
  MapMode = 5
  Placement = pos=(0,0,40) rot=(1,0,0;3.14159rad)
  Support = -> [DatumPlane015]
  sketch-geometry (12):
    g0: LineSegment StartX=104 StartY=-85 StartZ=0 EndX=114 EndY=-85 EndZ=0
    g1: LineSegment StartX=114 StartY=-85 StartZ=0 EndX=114 EndY=-95 EndZ=0
    g2: LineSegment StartX=114 StartY=-95 StartZ=0 EndX=104 EndY=-95 EndZ=0
    g3: LineSegment StartX=104 StartY=-95 StartZ=0 EndX=104 EndY=-85 EndZ=0
    g4: LineSegment StartX=25 StartY=-85 StartZ=0 EndX=15 EndY=-85 EndZ=0
    g5: LineSegment StartX=15 StartY=-85 StartZ=0 EndX=15 EndY=-95 EndZ=0
    g6: LineSegment StartX=15 StartY=-95 StartZ=0 EndX=25 EndY=-95 EndZ=0
    g7: LineSegment StartX=25 StartY=-95 StartZ=0 EndX=25 EndY=-85 EndZ=0
    g8: LineSegment StartX=21.5 StartY=-25 StartZ=0 EndX=15 EndY=-25 EndZ=0
    g9: LineSegment StartX=15 StartY=-25 StartZ=0 EndX=15 EndY=-34 EndZ=0
    g10: LineSegment StartX=15 StartY=-34 StartZ=0 EndX=21.5 EndY=-34 EndZ=0
    g11: LineSegment StartX=21.5 StartY=-34 StartZ=0 EndX=21.5 EndY=-25 EndZ=0
  constraints (33):
    c: Coincident(g0,g1)
    c: Coincident(g1,g2)
    c: Coincident(g2,g3)
    c: Coincident(g3,g0)
    c: Horizontal(g0)
    c: Horizontal(g2)
    c: Vertical(g1)
    c: Vertical(g3)
    c: Coincident(g4,g5)
    c: Coincident(g5,g6)
    c: Coincident(g6,g7)
    c: Coincident(g7,g4)
    c: Horizontal(g4)
    c: Horizontal(g6)
    c: Vertical(g5)
    c: Vertical(g7)
    c: Coincident(g1,g-3)
    c: Coincident(g5,g-4)
    c: DistanceY(g3,g3) = 10
    c: DistanceY(g7,g7) = 10
    c: DistanceX(g0,g0) = 10
    c: DistanceX(g4,g4) = 10
    c: Coincident(g8,g9)
    c: Coincident(g9,g10)
    c: Coincident(g10,g11)
    c: Coincident(g11,g8)
    c: Horizontal(g8)
    c: Horizontal(g10)
    c: Vertical(g9)
    c: Vertical(g11)
    c: Coincident(g8,g-6)
    c: Coincident(g8,g-5)
    c: DistanceY(g11,g11) = 9
FEATURE [PartDesign::Pad] Pad010
  BaseFeature = -> Pad009
  Length = 5
  Length2 = 100
  Profile = -> Sketch025
  Type = 0
FEATURE [Sketcher::SketchObject] Sketch026
  ExternalGeometry = -> [Pad010]
  MapMode = 5
  Placement = pos=(0,0,0) rot=(1,0,0;3.14159rad)
  Support = -> [Pad010]
  sketch-geometry (4):
    g0: LineSegment StartX=5 StartY=-5 StartZ=0 EndX=125 EndY=-5 EndZ=0
    g1: LineSegment StartX=125 StartY=-5 StartZ=0 EndX=125 EndY=-105 EndZ=0
    g2: LineSegment StartX=125 StartY=-105 StartZ=0 EndX=5 EndY=-105 EndZ=0
    g3: LineSegment StartX=5 StartY=-105 StartZ=0 EndX=5 EndY=-5 EndZ=0
  constraints (12):
    c: Coincident(g0,g1)
    c: Coincident(g1,g2)
    c: Coincident(g2,g3)
    c: Coincident(g3,g0)
    c: Horizontal(g0)
    c: Horizontal(g2)
    c: Vertical(g1)
    c: Vertical(g3)
    c: DistanceX(g-1,g0) = 5
    c: DistanceY(g0,g-1) = 5
    c: DistanceY(g3,g3) = 100
    c: DistanceX(g0,g0) = 120
FEATURE [Sketcher::SketchObject] Sketch027
  ExternalGeometry = -> [Pad010]
  MapMode = 5
  Placement = pos=(0,0,0) rot=(1,0,0;3.14159rad)
  Support = -> [Pad010]
  sketch-geometry (4):
    g0: LineSegment StartX=21.5 StartY=-15.2697 StartZ=0 EndX=30 EndY=-15.2697 EndZ=0
    g1: LineSegment StartX=30 StartY=-15.2697 StartZ=0 EndX=30 EndY=-25 EndZ=0
    g2: LineSegment StartX=30 StartY=-25 StartZ=0 EndX=21.5 EndY=-25 EndZ=0
    g3: LineSegment StartX=21.5 StartY=-25 StartZ=0 EndX=21.5 EndY=-15.2697 EndZ=0
  constraints (11):
    c: Coincident(g0,g1)
    c: Coincident(g1,g2)
    c: Coincident(g2,g3)
    c: Coincident(g3,g0)
    c: Horizontal(g0)
    c: Horizontal(g2)
    c: Vertical(g1)
    c: Vertical(g3)
    c: Coincident(g0,g-5)
    c: Coincident(g-3,g1)
    c: Coincident(g2,g-4)
FEATURE [PartDesign::Pocket] Pocket027
  BaseFeature = -> Pad010
  Length = 48
  Length2 = 100
  Profile = -> Sketch027
  Type = 0
FEATURE [PartDesign::Pocket] Pocket028
  BaseFeature = -> Pocket027
  Length = 6
  Length2 = 100
  Profile = -> Sketch026
  Type = 0
FEATURE [Sketcher::SketchObject] Sketch028
  ExternalGeometry = -> [Pocket028]
  MapMode = 5
  Placement = pos=(0,0,6) rot=(1,0,0;3.14159rad)
  Support = -> [Pocket028]
  sketch-geometry (4):
    g0: LineSegment StartX=75 StartY=-8.5 StartZ=0 EndX=108 EndY=-8.5 EndZ=0
    g1: LineSegment StartX=108 StartY=-8.5 StartZ=0 EndX=108 EndY=-10 EndZ=0
    g2: LineSegment StartX=108 StartY=-10 StartZ=0 EndX=75 EndY=-10 EndZ=0
    g3: LineSegment StartX=75 StartY=-10 StartZ=0 EndX=75 EndY=-8.5 EndZ=0
  constraints (11):
    c: Coincident(g0,g1)
    c: Coincident(g1,g2)
    c: Coincident(g2,g3)
    c: Coincident(g3,g0)
    c: Horizontal(g0)
    c: Horizontal(g2)
    c: Vertical(g1)
    c: Vertical(g3)
    c: Coincident(g-4,g2)
    c: Coincident(g1,g-3)
    c: DistanceY(g1,g1) = 1.5
FEATURE [PartDesign::Pocket] Pocket029
  BaseFeature = -> Pocket028
  Length = 42
  Length2 = 100
  Profile = -> Sketch028
  Type = 0
FEATURE [PartDesign::Pocket] Pocket030
  BaseFeature = -> Pocket029
  Length = 2
  Length2 = 100
  Profile = -> Pocket029 [Face44]
  Type = 0
FEATURE [PartDesign::Fillet] Fillet007
  Base = -> Pocket030 [Edge48]
  BaseFeature = -> Pocket030
  Radius = 3
FEATURE [PartDesign::Fillet] Fillet008
  Base = -> Fillet007 [Edge4]
  BaseFeature = -> Fillet007
  Radius = 4
FEATURE [PartDesign::Plane] DatumPlane016
  MapMode = 5
  Placement = pos=(0,0,40) rot=(1,0,0;3.14159rad)
  Support = -> [Fillet008]
FEATURE [Sketcher::SketchObject] Sketch029
  ExternalGeometry = -> [Fillet008]
  MapMode = 5
  Placement = pos=(0,0,40) rot=(1,0,0;3.14159rad)
  Support = -> [DatumPlane016]
  sketch-geometry (8):
    g0: LineSegment StartX=62.5 StartY=-41 StartZ=0 EndX=67.5 EndY=-41 EndZ=0
    g1: LineSegment StartX=67.5 StartY=-41 StartZ=0 EndX=67.5 EndY=-46 EndZ=0
    g2: LineSegment StartX=67.5 StartY=-46 StartZ=0 EndX=62.5 EndY=-46 EndZ=0
    g3: LineSegment StartX=62.5 StartY=-46 StartZ=0 EndX=62.5 EndY=-41 EndZ=0
    g4: LineSegment StartX=62.5 StartY=-84 StartZ=0 EndX=67.5 EndY=-84 EndZ=0
    g5: LineSegment StartX=67.5 StartY=-84 StartZ=0 EndX=67.5 EndY=-89 EndZ=0
    g6: LineSegment StartX=67.5 StartY=-89 StartZ=0 EndX=62.5 EndY=-89 EndZ=0
    g7: LineSegment StartX=62.5 StartY=-89 StartZ=0 EndX=62.5 EndY=-84 EndZ=0
  constraints (24):
    c: Coincident(g0,g1)
    c: Coincident(g1,g2)
    c: Coincident(g2,g3)
    c: Coincident(g3,g0)
    c: Horizontal(g0)
    c: Horizontal(g2)
    c: Vertical(g1)
    c: Vertical(g3)
    c: Coincident(g4,g5)
    c: Coincident(g5,g6)
    c: Coincident(g6,g7)
    c: Coincident(g7,g4)
    c: Horizontal(g4)
    c: Horizontal(g6)
    c: Vertical(g5)
    c: Vertical(g7)
    c: DistanceX(g0,g0) = 5
    c: DistanceX(g6,g6) = 5
    c: DistanceY(g1,g1) = 5
    c: DistanceY(g5,g5) = 5
    c: DistanceX(g0,g-4) = 2.5
    c: DistanceX(g4,g-4) = 2.5
    c: DistanceY(g-4,g1) = 19
    c: DistanceY(g4,g-4) = 19
FEATURE [PartDesign::Pocket] Pocket031
  BaseFeature = -> Fillet008
  Length = 20
  Length2 = 100
  Profile = -> Sketch029
  Type = 0
FEATURE [Sketcher::SketchObject] Sketch030
  ExternalGeometry = -> [Pocket031]
  MapMode = 5
  Placement = pos=(0,0,8) rot=(1,0,0;3.14159rad)
  Support = -> [Pocket031]
  sketch-geometry (4):
    g0: Circle CenterX=11.5 CenterY=-11.5 CenterZ=0 NormalX=0 NormalY=0 NormalZ=1 AngleXU=0 Radius=1.1
    g1: Circle CenterX=118.5 CenterY=-11.5 CenterZ=0 NormalX=0 NormalY=0 NormalZ=1 AngleXU=0 Radius=1.1
    g2: Circle CenterX=118.5 CenterY=-98.5 CenterZ=0 NormalX=0 NormalY=0 NormalZ=1 AngleXU=0 Radius=1.1
    g3: Circle CenterX=11.5 CenterY=-98.5 CenterZ=0 NormalX=0 NormalY=0 NormalZ=1 AngleXU=0 Radius=1.1
  constraints (12):
    c: Radius(g1) = 1.1
    c: Radius(g0) = 1.1
    c: Radius(g3) = 1.1
    c: Radius(g2) = 1.1
    c: DistanceX(g-3,g0) = 6.5
    c: DistanceY(g0,g-3) = 6.5
    c: DistanceX(g1,g-6) = 6.5
    c: DistanceX(g2,g-5) = 6.5
    c: DistanceX(g-4,g3) = 6.5
    c: DistanceY(g1,g-6) = 6.5
    c: DistanceY(g-5,g2) = 6.5
    c: DistanceY(g-4,g3) = 6.5
FEATURE [PartDesign::Pocket] Pocket032
  BaseFeature = -> Pocket031
  Length = 20
  Length2 = 100
  Profile = -> Sketch030
  Type = 0
FEATURE [PartDesign::Body] Body
  Group = -> [Sketch,DatumPlane,Sketch001,AdditiveLoft,DatumPlane001,Sketch002,Pocket,DatumPlane002,Sketch003,Pocket001,Sketch004,DatumPlane003,Sketch005,Pad,DatumPlane004,Sketch006,Pocket002,DatumPlane005,Sketch007,Pocket003,DatumPlane006,Sketch008,Sketch009,Pocket004,Chamfer,Fillet,Chamfer001,Fillet001,Fillet002,Fillet003,Fillet004,Fillet005,Fillet006,DatumPlane007,Sketch010,Pad001,DatumPlane008,Sketch011,+66 more]
  Origin = -> Origin
  Tip = -> Pocket032
FEATURE [Mesh::Feature] Mesh  label="NewDesign"
